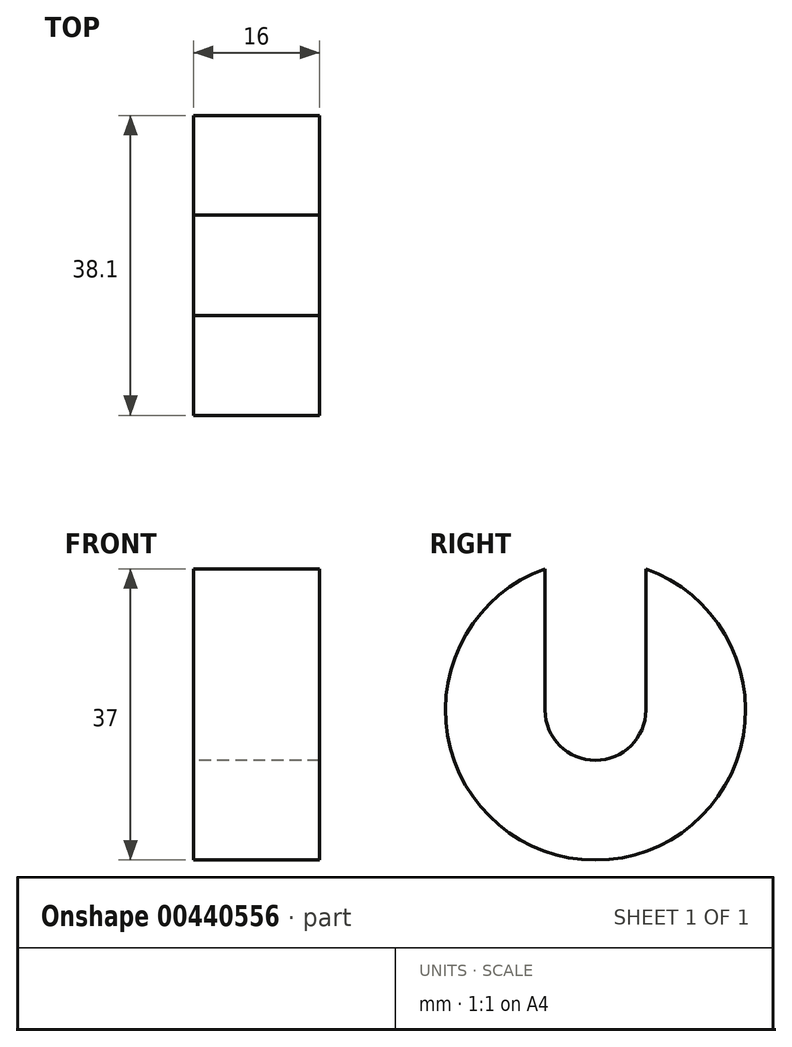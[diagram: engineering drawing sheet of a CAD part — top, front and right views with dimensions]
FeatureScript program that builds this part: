
annotation { "Feature Type Name" : "Feature", "Feature Type Description" : "" }
export const myFeature = defineFeature(function(context is Context, id is Id, definition is map)
    precondition{}
    {
        {
            var Q0;
            Q0=qCreatedBy(makeId("Right.planeOp"),FACE);
            var sketch = newSketch(context, id + "F0", { "sketchPlane" : qUnion([Q0])});
            skArc(sketch, "E0", {"start": v(-6.39, 0) * mm, "mid": v(0, -6.39) * mm, "end": v(6.39, 0) * mm});
            skCircle(sketch, "E1", {"center": v(0, 0) * mm, "radius": 19.05 * mm});
            skLineSegment(sketch, "E2", {"start": v(-6.39, 0) * mm, "end": v(-6.39, 25.27) * mm});
            skLineSegment(sketch, "E3", {"start": v(6.39, 0) * mm, "end": v(6.39, 25.14) * mm});
            skCircle(sketch, "E4", {"center": v(0, 0) * mm, "radius": 5.56 * mm, "construction": true});
            skSolve(sketch);
        }
        {
            var Q0;
            {var subQ0=sQuery(id+"F0.wireOp",EDGE,"E0");Q0=makeQuery(id+"F0.imprint","IMPRINT",FACE,{"disambiguationData":[TD([[makeQuery(id+"F0.imprint","IMPRINT",EDGE,{"derivedFrom":subQ0}),-1.0]])]});}
            extrude(context, id + "F1", {"entities" : qUnion([Q0]), "endBound" : BoundingType.SYMMETRIC, "depth" : 16 * mm});
        }
    });
